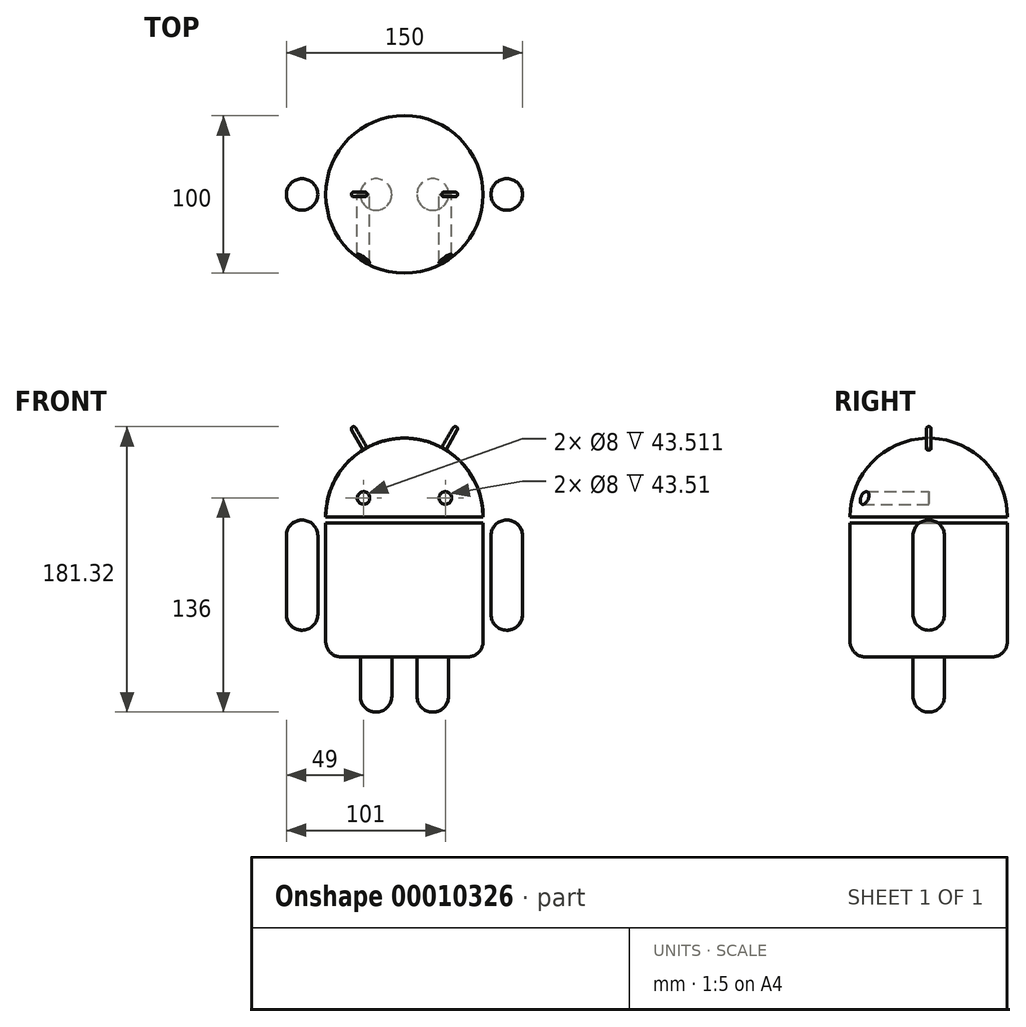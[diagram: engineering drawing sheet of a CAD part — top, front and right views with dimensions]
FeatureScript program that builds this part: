
annotation { "Feature Type Name" : "Feature", "Feature Type Description" : "" }
export const myFeature = defineFeature(function(context is Context, id is Id, definition is map)
    precondition{}
    {
        {
            var Q0;
            Q0=qCreatedBy(makeId("Front.planeOp"),FACE);
            var sketch = newSketch(context, id + "F0", { "sketchPlane" : qUnion([Q0])});
            skLineSegment(sketch, "E0", {"start": v(0, 63.5) * mm, "end": v(0, -112.89) * mm, "construction": true});
            skLineSegment(sketch, "E1", {"start": v(0, 0) * mm, "end": v(50, 0) * mm});
            skLineSegment(sketch, "E2", {"start": v(50, 0) * mm, "end": v(50, -75) * mm});
            skLineSegment(sketch, "E3", {"start": v(40, -85) * mm, "end": v(0, -85) * mm});
            skLineSegment(sketch, "E4", {"start": v(0, -85) * mm, "end": v(0, 0) * mm});
            skLineSegment(sketch, "E5", {"start": v(0, 4) * mm, "end": v(50, 4) * mm});
            skLineSegment(sketch, "E6", {"start": v(0, 4) * mm, "end": v(0, 54) * mm});
            skArc(sketch, "E7", {"start": v(50, 4) * mm, "mid": v(35.36, 39.36) * mm, "end": v(0, 54) * mm});
            skLineSegment(sketch, "E8", {"start": v(0, 54) * mm, "end": v(-42.59, 54) * mm, "construction": true});
            skPoint(sketch, "E9.visualSharp", {"position": v(50, -85) * mm});
            skArc(sketch, "E9.filletArc", {"start": v(40, -85) * mm, "mid": v(47.07, -82.07) * mm, "end": v(50, -75) * mm});
            skSolve(sketch);
        }
        {
            var Q0;
            Q0=makeQuery(id+"F0.imprint","IMPRINT",FACE,{"disambiguationData":[TD([[makeQuery(id+"F0.imprint","IMPRINT",EDGE,{"derivedFrom":sQuery(id+"F0.wireOp",EDGE,"E5")}),1.0]])]});
            var Q1;
            Q1=makeQuery(id+"F0.imprint","IMPRINT",FACE,{"disambiguationData":[TD([[makeQuery(id+"F0.imprint","IMPRINT",EDGE,{"derivedFrom":sQuery(id+"F0.wireOp",EDGE,"E1")}),-1.0]])]});
            var Q2;
            Q2=sQuery(id+"F0.wireOp",EDGE,"E0");
            revolve(context, id + "F1", {"entities" : qUnion([Q0, Q1]), "axis" : qUnion([Q2]), "revolveType" : RevolveType.FULL});
        }
        {
            var Q0;
            Q0=qCreatedBy(makeId("Front.planeOp"),FACE);
            var sketch = newSketch(context, id + "F2", { "sketchPlane" : qUnion([Q0])});
            skLineSegment(sketch, "E10", {"start": v(18, -77.06) * mm, "end": v(18, -138.1) * mm, "construction": true});
            skLineSegment(sketch, "E11", {"start": v(18, -85) * mm, "end": v(28, -85) * mm});
            skLineSegment(sketch, "E12", {"start": v(28, -85) * mm, "end": v(28, -110) * mm});
            skLineSegment(sketch, "E13", {"start": v(18, -120) * mm, "end": v(18, -120) * mm});
            skLineSegment(sketch, "E14", {"start": v(18, -120) * mm, "end": v(18, -85) * mm});
            skPoint(sketch, "E15.visualSharp", {"position": v(28, -120) * mm});
            skArc(sketch, "E15.filletArc", {"start": v(18, -120) * mm, "mid": v(25.07, -117.07) * mm, "end": v(28, -110) * mm});
            skSolve(sketch);
        }
        {
            var Q0;
            Q0=makeQuery(id+"F2.imprint","IMPRINT",FACE,{"disambiguationData":[TD([[makeQuery(id+"F2.imprint","IMPRINT",EDGE,{"derivedFrom":sQuery(id+"F2.wireOp",EDGE,"E11")}),-1.0]])]});
            var Q1;
            Q1=sQuery(id+"F2.wireOp",EDGE,"E10");
            revolve(context, id + "F3", {"operationType" : NewBodyOperationType.ADD, "entities" : qUnion([Q0]), "axis" : qUnion([Q1]), "revolveType" : RevolveType.FULL});
        }
        {
            var Q0;
            Q0=qCreatedBy(makeId("Front.planeOp"),FACE);
            var sketch = newSketch(context, id + "F4", { "sketchPlane" : qUnion([Q0])});
            skLineSegment(sketch, "E16", {"start": v(65, 12.15) * mm, "end": v(65, -85.61) * mm, "construction": true});
            skLineSegment(sketch, "E17.bottom", {"start": v(65, -68) * mm, "end": v(65, -68) * mm});
            skLineSegment(sketch, "E17.top", {"start": v(65, 2) * mm, "end": v(65, 2) * mm});
            skLineSegment(sketch, "E17.left", {"start": v(65, -68) * mm, "end": v(65, 2) * mm});
            skLineSegment(sketch, "E17.right", {"start": v(75, -58) * mm, "end": v(75, -8) * mm});
            skPoint(sketch, "E18.visualSharp", {"position": v(75, -68) * mm});
            skArc(sketch, "E18.filletArc", {"start": v(65, -68) * mm, "mid": v(72.07, -65.07) * mm, "end": v(75, -58) * mm});
            skPoint(sketch, "E19.visualSharp", {"position": v(75, 2) * mm});
            skArc(sketch, "E19.filletArc", {"start": v(75, -8) * mm, "mid": v(72.07, -0.93) * mm, "end": v(65, 2) * mm});
            skSolve(sketch);
        }
        {
            var Q0;
            Q0 = qSketchRegion(id + "F4", true);
            var Q1;
            Q1=sQuery(id+"F4.wireOp",EDGE,"E16");
            revolve(context, id + "F5", {"entities" : qUnion([Q0]), "axis" : qUnion([Q1]), "revolveType" : RevolveType.FULL});
        }
        {
            var Q0;
            Q0=qCreatedBy(makeId("Front.planeOp"),FACE);
            var sketch = newSketch(context, id + "F6", { "sketchPlane" : qUnion([Q0])});
            skLineSegment(sketch, "E20", {"start": v(0, 3.96) * mm, "end": v(16.28, 32.17) * mm, "construction": true});
            skLineSegment(sketch, "E21", {"start": v(23, 43.8) * mm, "end": v(24.3, 43.05) * mm});
            skLineSegment(sketch, "E22", {"start": v(24.3, 43.05) * mm, "end": v(33.55, 59.07) * mm});
            skLineSegment(sketch, "E23", {"start": v(33, 61.12) * mm, "end": v(33, 61.12) * mm});
            skLineSegment(sketch, "E24", {"start": v(33, 61.12) * mm, "end": v(23, 43.8) * mm});
            skPoint(sketch, "E25.visualSharp", {"position": v(34.3, 60.37) * mm});
            skArc(sketch, "E25.filletArc", {"start": v(33.55, 59.07) * mm, "mid": v(33.7, 60.2) * mm, "end": v(33, 61.12) * mm});
            skSolve(sketch);
        }
        {
            var Q0;
            Q0 = qSketchRegion(id + "F6", true);
            var Q1;
            Q1=sQuery(id+"F6.wireOp",EDGE,"E20");
            revolve(context, id + "F7", {"operationType" : NewBodyOperationType.ADD, "entities" : qUnion([Q0]), "axis" : qUnion([Q1]), "revolveType" : RevolveType.FULL});
        }
        {
            var Q0;
            Q0=makeQuery(id+"F5.opRevolve","SWEPT_BODY",BODY,{"disambiguationData":[OSD([sQuery(id+"F4.wireOp",EDGE,"E17.left"),sQuery(id+"F4.wireOp",EDGE,"E17.right"),sQuery(id+"F4.wireOp",EDGE,"E18.filletArc"),sQuery(id+"F4.wireOp",EDGE,"E19.filletArc")])]});
            var Q1;
            Q1=makeQuery(id+"F1.opRevolve","SWEPT_BODY",BODY,{"disambiguationData":[OSD([sQuery(id+"F0.wireOp",EDGE,"E1"),sQuery(id+"F0.wireOp",EDGE,"E2"),sQuery(id+"F0.wireOp",EDGE,"E3"),sQuery(id+"F0.wireOp",EDGE,"E4"),sQuery(id+"F0.wireOp",EDGE,"E9.filletArc")])]});
            var Q2;
            Q2=makeQuery(id+"F1.opRevolve","SWEPT_BODY",BODY,{"disambiguationData":[OSD([sQuery(id+"F0.wireOp",EDGE,"E5"),sQuery(id+"F0.wireOp",EDGE,"E6"),sQuery(id+"F0.wireOp",EDGE,"E7")])]});
            var Q3;
            Q3=qCreatedBy(makeId("Right.planeOp"),FACE);
            mirror(context, id + "F8", {"entities" : qUnion([Q0, Q1, Q2]), "mirrorPlane" : qUnion([Q3])});
        }
        {
            var Q0;
            Q0=qCreatedBy(makeId("Front.planeOp"),FACE);
            var sketch = newSketch(context, id + "F9", { "sketchPlane" : qUnion([Q0])});
            skCircle(sketch, "E26", {"center": v(26, 16) * mm, "radius": 4 * mm});
            skCircle(sketch, "E27", {"center": v(-26, 16) * mm, "radius": 4 * mm});
            skSolve(sketch);
        }
        {
            var Q0;
            Q0 = qSketchRegion(id + "F9", true);
            extrude(context, id + "F10", {"entities" : qUnion([Q0]), "operationType" : NewBodyOperationType.REMOVE, "depth" : 60 * mm});
        }
    });
